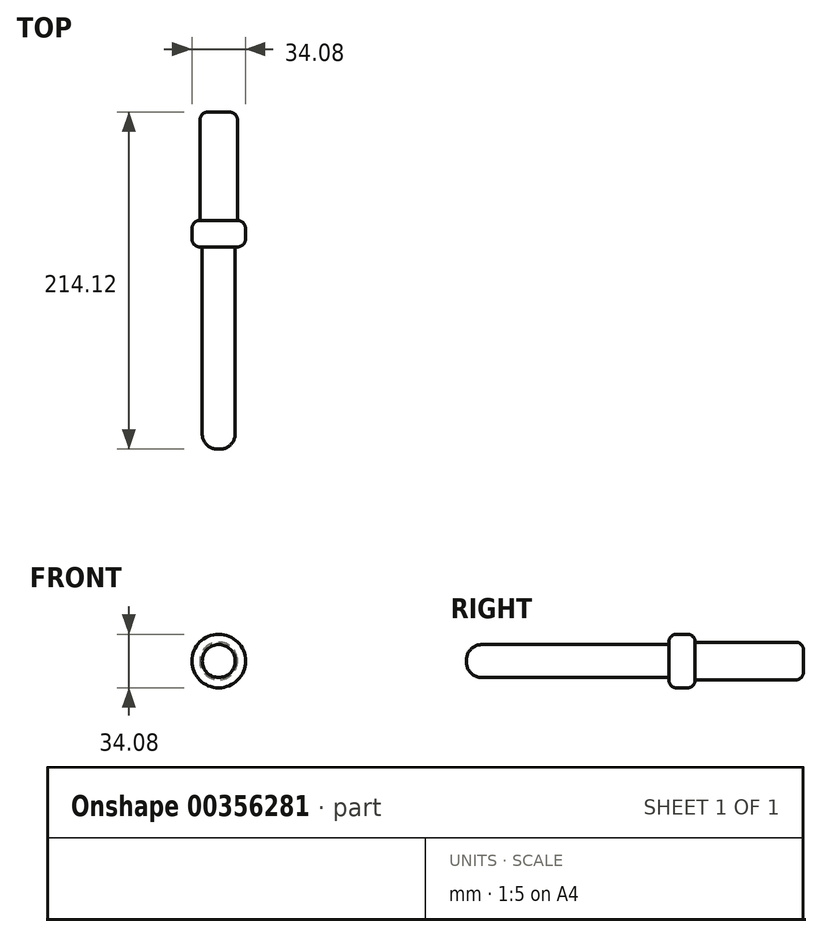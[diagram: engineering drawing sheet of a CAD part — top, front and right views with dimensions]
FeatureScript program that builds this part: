
annotation { "Feature Type Name" : "Feature", "Feature Type Description" : "" }
export const myFeature = defineFeature(function(context is Context, id is Id, definition is map)
    precondition{}
    {
        {
            var Q0;
            Q0=qCreatedBy(makeId("Front.planeOp"),FACE);
            var sketch = newSketch(context, id + "F0", { "sketchPlane" : qUnion([Q0])});
            skCircle(sketch, "E0", {"center": v(0, 0) * mm, "radius": 10.48 * mm});
            skSolve(sketch);
        }
        {
            var Q0;
            Q0=makeQuery(id+"F0.imprint","IMPRINT",FACE,{"disambiguationData":[TD([[makeQuery(id+"F0.imprint","IMPRINT",EDGE,{"derivedFrom":sQuery(id+"F0.wireOp",EDGE,"E0")}),1.0]])]});
            extrude(context, id + "F1", {"entities" : qUnion([Q0]), "depth" : 128.52 * mm});
        }
        {
            var Q0;
            Q0=makeQuery(id+"F1.opExtrude","CAP_EDGE",EDGE,{"disambiguationData":[OSD([sQuery(id+"F0.wireOp",EDGE,"E0")])],"isStart":false});
            fillet(context, id + "F2", {"entities" : qUnion([Q0]), "radius" : 9.8 * mm, "tangentPropagation" : true, "allowEdgeOverflow" : false});
        }
        {
            var Q0;
            Q0=qCreatedBy(makeId("Front.planeOp"),FACE);
            var sketch = newSketch(context, id + "F3", { "sketchPlane" : qUnion([Q0])});
            skCircle(sketch, "E1", {"center": v(0, 0) * mm, "radius": 17.04 * mm});
            skSolve(sketch);
        }
        {
            var Q0;
            Q0=makeQuery(id+"F3.imprint","IMPRINT",FACE,{"disambiguationData":[TD([[makeQuery(id+"F3.imprint","IMPRINT",EDGE,{"derivedFrom":sQuery(id+"F3.wireOp",EDGE,"E1")}),1.0]])]});
            extrude(context, id + "F4", {"entities" : qUnion([Q0]), "operationType" : NewBodyOperationType.ADD, "oppositeDirection" : true, "depth" : 16.76 * mm});
        }
        {
            var Q0;
            Q0=makeQuery(id+"F4.opExtrude","CAP_EDGE",EDGE,{"disambiguationData":[OSD([sQuery(id+"F3.wireOp",EDGE,"E1")])],"isStart":false});
            fillet(context, id + "F5", {"entities" : qUnion([Q0]), "radius" : 5.08 * mm, "tangentPropagation" : true, "allowEdgeOverflow" : false});
        }
        {
            var Q0;
            Q0=makeQuery(id+"F4.opExtrude","CAP_EDGE",EDGE,{"disambiguationData":[OSD([sQuery(id+"F3.wireOp",EDGE,"E1")])],"isStart":true});
            fillet(context, id + "F6", {"entities" : qUnion([Q0]), "radius" : 5.08 * mm, "tangentPropagation" : true, "allowEdgeOverflow" : false});
        }
        {
            var Q0;
            Q0=makeQuery(id+"F4.opExtrude","CAP_FACE",FACE,{"disambiguationData":[OSD([sQuery(id+"F3.wireOp",EDGE,"E1")])],"isStart":false});
            extrude(context, id + "F7", {"entities" : qUnion([Q0]), "operationType" : NewBodyOperationType.ADD, "depth" : 68.83 * mm});
        }
        {
            var Q0;
            Q0=makeQuery(id+"F7.opExtrude","CAP_EDGE",EDGE,{"disambiguationData":[OSD([sQuery(id+"F3.wireOp",EDGE,"E1")])],"isStart":false});
            fillet(context, id + "F8", {"entities" : qUnion([Q0]), "radius" : 5.08 * mm, "tangentPropagation" : true, "allowEdgeOverflow" : false});
        }
    });
